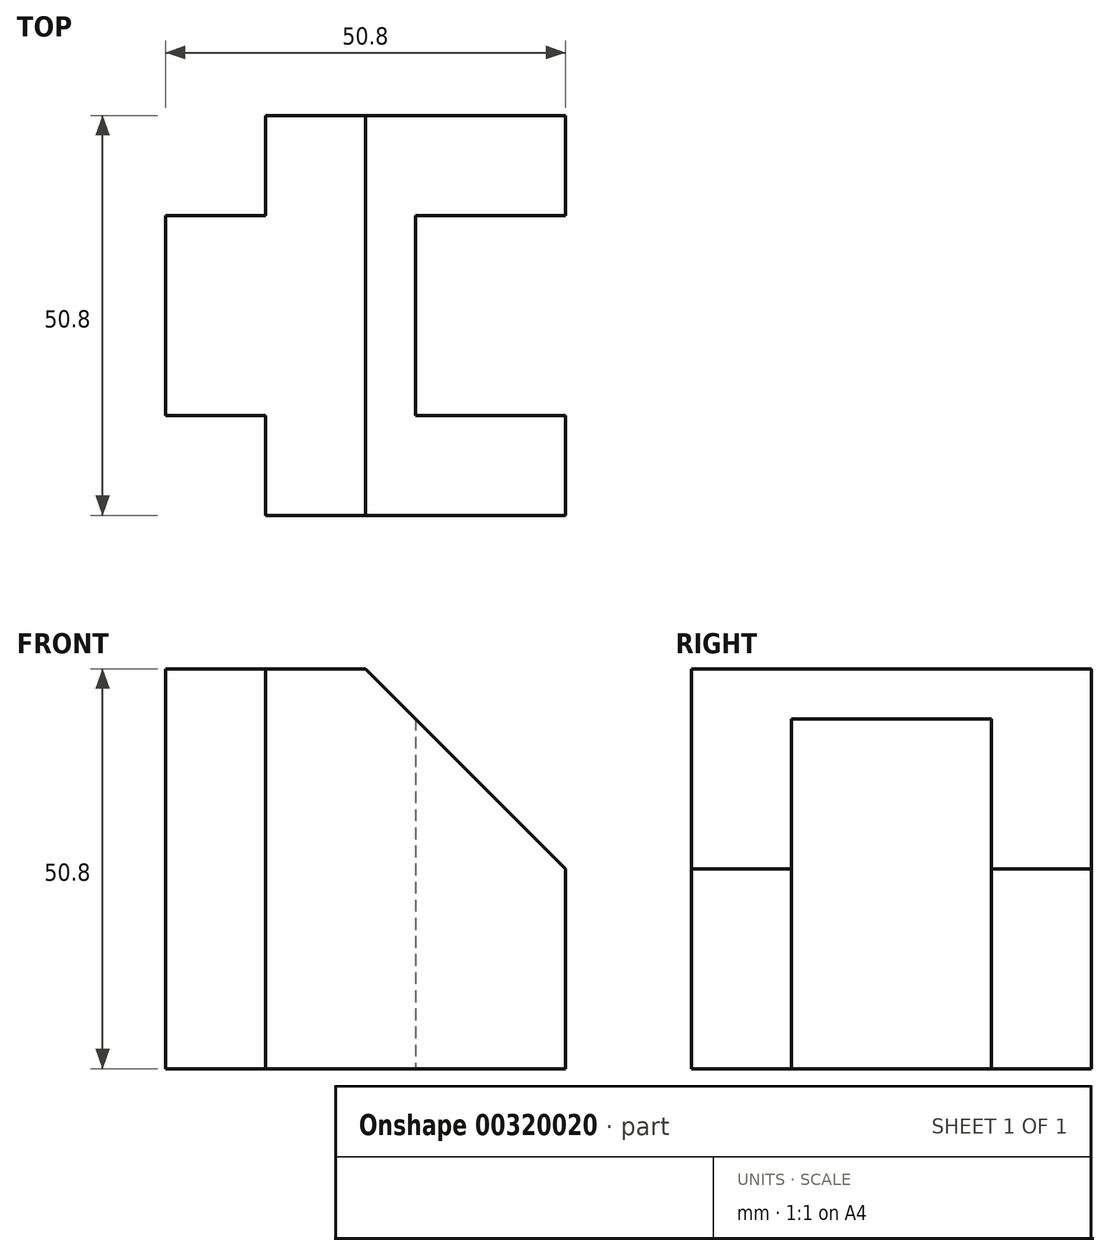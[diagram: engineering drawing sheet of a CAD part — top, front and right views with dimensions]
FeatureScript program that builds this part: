
annotation { "Feature Type Name" : "Feature", "Feature Type Description" : "" }
export const myFeature = defineFeature(function(context is Context, id is Id, definition is map)
    precondition{}
    {
        {
            var Q0;
            Q0=qCreatedBy(makeId("Front.planeOp"),FACE);
            var sketch = newSketch(context, id + "F0", { "sketchPlane" : qUnion([Q0])});
            skLineSegment(sketch, "E0", {"start": v(0, 0) * mm, "end": v(0, 50.8) * mm});
            skLineSegment(sketch, "E1", {"start": v(0, 50.8) * mm, "end": v(12.7, 50.8) * mm});
            skLineSegment(sketch, "E2", {"start": v(12.7, 50.8) * mm, "end": v(38.1, 25.4) * mm});
            skLineSegment(sketch, "E3", {"start": v(38.1, 25.4) * mm, "end": v(38.1, 0) * mm});
            skLineSegment(sketch, "E4", {"start": v(38.1, 0) * mm, "end": v(0, 0) * mm});
            skSolve(sketch);
        }
        {
            var Q0;
            Q0 = qSketchRegion(id + "F0", true);
            extrude(context, id + "F1", {"entities" : qUnion([Q0]), "depth" : 12.7 * mm});
        }
        {
            var Q0;
            Q0=makeQuery(id+"F1.opExtrude","CAP_FACE",FACE,{"disambiguationData":[OSD([sQuery(id+"F0.wireOp",EDGE,"E0"),sQuery(id+"F0.wireOp",EDGE,"E1"),sQuery(id+"F0.wireOp",EDGE,"E2"),sQuery(id+"F0.wireOp",EDGE,"E3"),sQuery(id+"F0.wireOp",EDGE,"E4")])],"isStart":true});
            var sketch = newSketch(context, id + "F2", { "sketchPlane" : qUnion([Q0])});
            skLineSegment(sketch, "E5", {"start": v(-19.05, 44.45) * mm, "end": v(-12.7, 50.8) * mm});
            skLineSegment(sketch, "E6", {"start": v(-12.7, 50.8) * mm, "end": v(0, 50.8) * mm});
            skLineSegment(sketch, "E7", {"start": v(0, 50.8) * mm, "end": v(12.7, 50.8) * mm});
            skLineSegment(sketch, "E8", {"start": v(12.7, 50.8) * mm, "end": v(12.7, 0) * mm});
            skLineSegment(sketch, "E9", {"start": v(12.7, 0) * mm, "end": v(0, 0) * mm});
            skLineSegment(sketch, "E10", {"start": v(0, 0) * mm, "end": v(-19.05, 0) * mm});
            skLineSegment(sketch, "E11", {"start": v(-19.05, 44.45) * mm, "end": v(-19.05, 0) * mm});
            skSolve(sketch);
        }
        {
            var Q0;
            Q0 = qSketchRegion(id + "F2", true);
            extrude(context, id + "F3", {"entities" : qUnion([Q0]), "operationType" : NewBodyOperationType.ADD, "depth" : 25.4 * mm});
        }
        {
            var Q0;
            Q0=makeQuery(id+"F3.opExtrude","CAP_FACE",FACE,{"disambiguationData":[OSD([sQuery(id+"F2.wireOp",EDGE,"E5"),sQuery(id+"F2.wireOp",EDGE,"E6"),sQuery(id+"F2.wireOp",EDGE,"E7"),sQuery(id+"F2.wireOp",EDGE,"E8"),sQuery(id+"F2.wireOp",EDGE,"E9"),sQuery(id+"F2.wireOp",EDGE,"E10"),sQuery(id+"F2.wireOp",EDGE,"E11")])],"isStart":false});
            var sketch = newSketch(context, id + "F4", { "sketchPlane" : qUnion([Q0])});
            skLineSegment(sketch, "E12", {"start": v(-12.7, 50.8) * mm, "end": v(-38.1, 25.4) * mm});
            skLineSegment(sketch, "E13", {"start": v(-38.1, 25.4) * mm, "end": v(-38.1, 0) * mm});
            skLineSegment(sketch, "E14", {"start": v(-38.1, 0) * mm, "end": v(0, 0) * mm});
            skLineSegment(sketch, "E15", {"start": v(0, 0) * mm, "end": v(0, 50.8) * mm});
            skLineSegment(sketch, "E16", {"start": v(0, 50.8) * mm, "end": v(-12.7, 50.8) * mm});
            skSolve(sketch);
        }
        {
            var Q0;
            Q0 = qSketchRegion(id + "F4", true);
            extrude(context, id + "F5", {"entities" : qUnion([Q0]), "operationType" : NewBodyOperationType.ADD, "depth" : 12.7 * mm});
        }
    });
